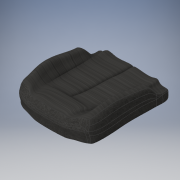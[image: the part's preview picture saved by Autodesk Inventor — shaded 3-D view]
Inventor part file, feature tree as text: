
AUTODESK INVENTOR PART (.ipt)
format: ipt  version: 2019 (Build 230136000, 136)  size: 1,995,776 bytes
history: native  units: in
note: dims shown in document units (in); Inventor stores cm internally (conversion verified against a paired STEP export)
features: sketch x13, other x10, extrude x10, fillet x6, plane x5, projected_geometry x3, mirror x2
ambient origin geometry x8: Origin, YZ Plane, XZ Plane, XY Plane, X Axis, Y Axis, Z Axis, Center Point
bodies: Solid1 (feature_tree)
feature tree (49):
  other  "Blocks"
  plane  "Work Plane1"
  plane  "Work Plane2"
  plane  "Work Plane3"
  plane  "Work Plane4"
  other  "Form1"
  sketch  "Sketch1"  dims[d0=7.874in d3=3.248in]
  sketch  "Sketch3"  dims[d4=9.8425in d5=-0.1772in]
  sketch  "Sketch4"  dims[d11=13.3858in d12=0.0in d13=0.7874in]
  sketch  "Sketch5"  dims[d14=23.622in d15=1.9685in]
  sketch  "Sketch8"  dims[d16=0.0in d17=0.0in d18=0.3937in]
  extrude  "Extrusion3"  Depth=3.248in
  extrude  "Extrusion4"  [1 undecoded]
  extrude  "Extrusion5"  Depth=0.7874in
  extrude  "Extrusion7"  Depth=1.9685in
  mirror  "Mirror1"
  extrude  "Extrusion8"  Depth=0.3937in
  extrude  "Extrusion9"  TaperAngle=0.0deg  [1 undecoded]
  mirror  "Mirror2"
  extrude  "Extrusion10"  Depth=6.6929in
  fillet  "Fillet1"  Radius=2.3622in
  fillet  "Fillet2"  Radius=3.937in
  fillet  "Fillet3"  Radius=0.5906in
  fillet  "Fillet4"  Radius=0.0394in
  fillet  "Fillet5"  Radius=1.1811in
  extrude  "Extrusion11"  Depth=0.7874in
  extrude  "Extrusion12"  Depth=0.1969in
  fillet  "Fillet6"  Radius=0.1969in
  plane  "Work Plane5"
  extrude  "Extrusion13"  Depth=0.3937in TaperAngle=0.0deg
  other  "Block1"
  other  "Block2"
  other  "Block3"
  other  "Block4"
  other  "Block5"
  sketch  "Sketch9"  dims[d20=1.1811in d21=0.0in d24=0.0in d25=0.0in]
  sketch  "Sketch10"  dims[d26=0.7874in d27=6.6929in d28=2.3622in d29=0.0in d30=3.937in d31=0.5906in d32=0.0394in d33=1.1811in d34=0.0in]
  other  "Block6"
  projected_geometry  "Projected Loop1"
  sketch  "Sketch12"  dims[d35=1.1811in d36=0.0in d37=0.7874in]
  sketch  "Sketch13"  dims[d38=0.7874in d39=0.1969in d40=0.1969in]
  sketch  "Sketch14"  dims[d41=0.1969in d42=0.3937in d43=0.0in]
  projected_geometry  "Projected Loop3"
  sketch  "Sketch15"  dims[d44=0.5906in d45=0.1969in d46=0.0in d47=0.0in]
  sketch  "Sketch16"  dims[d48=0.0787in]
  projected_geometry  "Projected Loop4"
  sketch  "Sketch17"  dims[d49=-9.8425in d50=2.1654in d51=0.0in d52=1.1024in d53=1.1024in]
  other  "Block2:1"
  other  "Block3:1"
note: 2 required parameter values undecoded (feature->parameter linkage not recoverable at this tier; creation-order binding heuristic only, values carry confidence <= 0.55)
